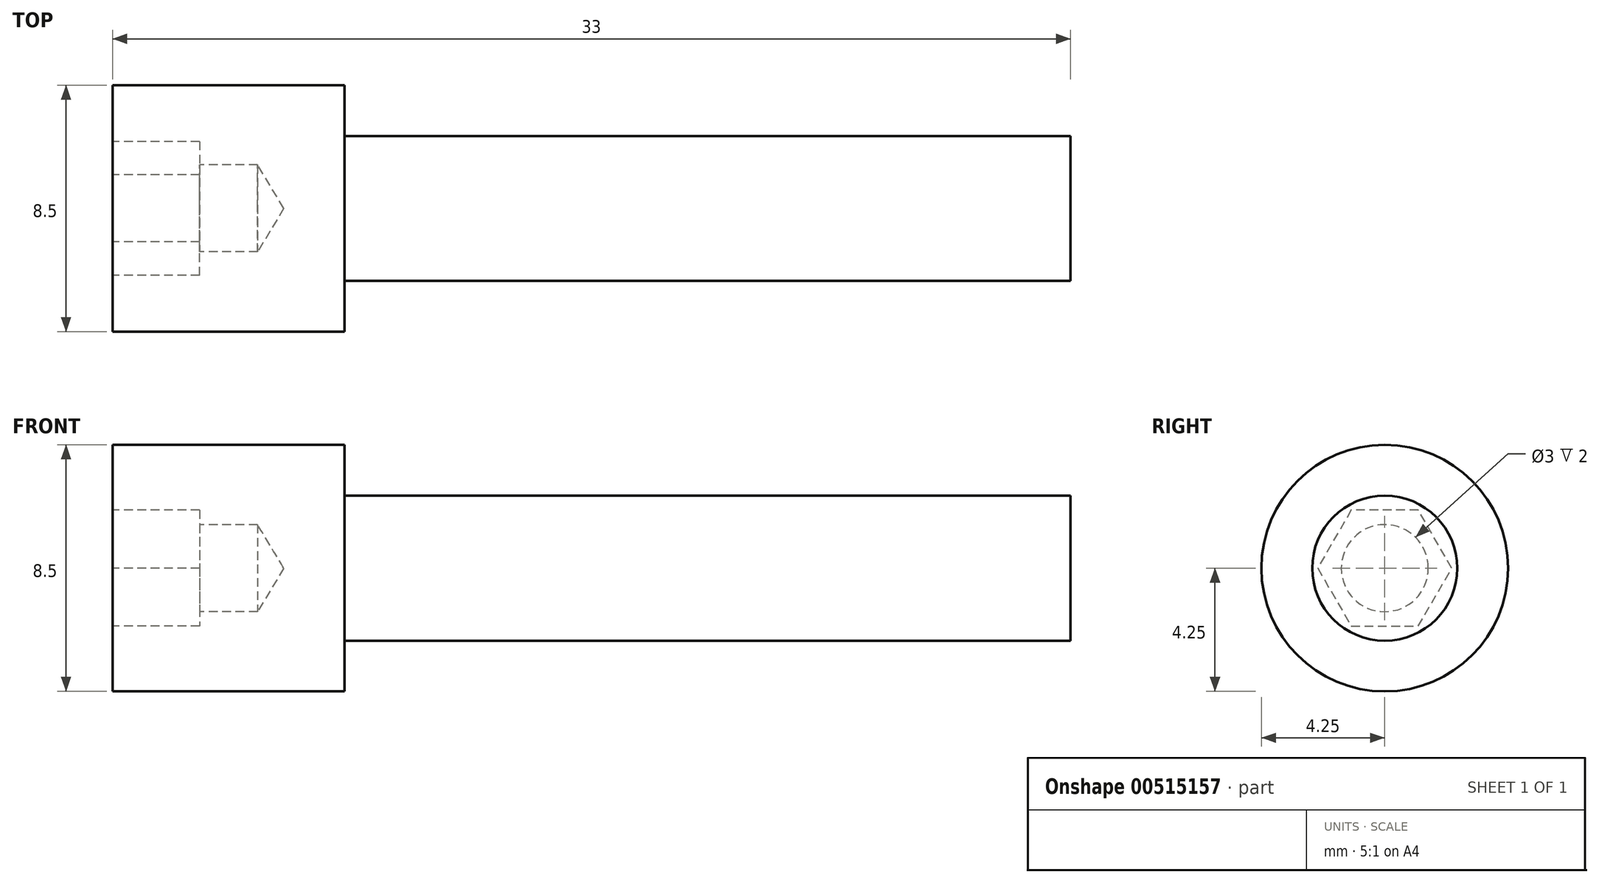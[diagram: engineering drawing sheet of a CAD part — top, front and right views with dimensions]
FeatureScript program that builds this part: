
annotation { "Feature Type Name" : "Feature", "Feature Type Description" : "" }
export const myFeature = defineFeature(function(context is Context, id is Id, definition is map)
    precondition{}
    {
        {
            var Q0;
            Q0=qCreatedBy(makeId("Front.planeOp"),FACE);
            var sketch = newSketch(context, id + "F0", { "sketchPlane" : qUnion([Q0])});
            skLineSegment(sketch, "E0", {"start": v(-8, 0) * mm, "end": v(-8, 4.25) * mm});
            skLineSegment(sketch, "E1", {"start": v(-8, 4.25) * mm, "end": v(0, 4.25) * mm});
            skLineSegment(sketch, "E2", {"start": v(0, 4.25) * mm, "end": v(0, 2.5) * mm});
            skLineSegment(sketch, "E3", {"start": v(0, 2.5) * mm, "end": v(25, 2.5) * mm});
            skLineSegment(sketch, "E4", {"start": v(25, 2.5) * mm, "end": v(25, 0) * mm});
            skLineSegment(sketch, "E5", {"start": v(25, 0) * mm, "end": v(-8, 0) * mm});
            skSolve(sketch);
        }
        {
            var Q0;
            Q0=makeQuery(id+"F0.imprint","IMPRINT",FACE,{"disambiguationData":[TD([[makeQuery(id+"F0.imprint","IMPRINT",EDGE,{"derivedFrom":sQuery(id+"F0.wireOp",EDGE,"E0")}),-1.0]])]});
            var Q1;
            Q1=sQuery(id+"F0.wireOp",EDGE,"E5");
            revolve(context, id + "F1", {"entities" : qUnion([Q0]), "axis" : qUnion([Q1]), "revolveType" : RevolveType.FULL});
        }
        {
            var Q0;
            Q0=makeQuery(id+"F1.opRevolve","SWEPT_FACE",FACE,{"disambiguationData":[OSD([sQuery(id+"F0.wireOp",EDGE,"E0")])]});
            var sketch = newSketch(context, id + "F2", { "sketchPlane" : qUnion([Q0])});
            skCircle(sketch, "E6.cCircle", {"center": v(0, 0) * mm, "radius": 2 * mm, "construction": true});
            skLineSegment(sketch, "E6.0", {"start": v(1.15, -2) * mm, "end": v(-1.15, -2) * mm});
            skLineSegment(sketch, "E6.1", {"start": v(-1.15, -2) * mm, "end": v(-2.3, 0) * mm});
            skLineSegment(sketch, "E6.2", {"start": v(-2.3, 0) * mm, "end": v(-1.15, 2) * mm});
            skLineSegment(sketch, "E6.3", {"start": v(-1.15, 2) * mm, "end": v(1.15, 2) * mm});
            skLineSegment(sketch, "E6.4", {"start": v(1.15, 2) * mm, "end": v(2.3, 0) * mm});
            skLineSegment(sketch, "E6.5", {"start": v(2.3, 0) * mm, "end": v(1.15, -2) * mm});
            skPoint(sketch, "E6.0.midPoint", {"position": v(0, -2) * mm});
            skSolve(sketch);
        }
        {
            var Q0;
            Q0=sQuery(id+"F2.wireOp",VERTEX,"E6.cCircle.center");
            var Q1;
            Q1=makeQuery(id+"F1.opRevolve","SWEPT_BODY",BODY,{"disambiguationData":[OSD([sQuery(id+"F0.wireOp",EDGE,"E0"),sQuery(id+"F0.wireOp",EDGE,"E1"),sQuery(id+"F0.wireOp",EDGE,"E2"),sQuery(id+"F0.wireOp",EDGE,"E3"),sQuery(id+"F0.wireOp",EDGE,"E4"),sQuery(id+"F0.wireOp",EDGE,"E5")])]});
            hole(context, id + "F3", {"style" : HoleStyle.SIMPLE, "endStyle" : HoleEndStyle.BLIND, "holeDiameter" : 3 * mm, "holeDepth" : 5 * mm, "isTappedThrough" : true, "tappedDepth" : 10.1 * mm, "tapClearance" : 3, "locations" : qUnion([Q0]), "scope" : qUnion([Q1])});
        }
        {
            var Q0;
            Q0=makeQuery(id+"F2.imprint","IMPRINT",FACE,{"disambiguationData":[TD([[makeQuery(id+"F2.imprint","IMPRINT",EDGE,{"derivedFrom":sQuery(id+"F2.wireOp",EDGE,"E6.0")}),-1.0]])]});
            extrude(context, id + "F4", {"entities" : qUnion([Q0]), "operationType" : NewBodyOperationType.REMOVE, "oppositeDirection" : true, "depth" : 3 * mm, "offsetDistance" : 25 * mm});
        }
    });
